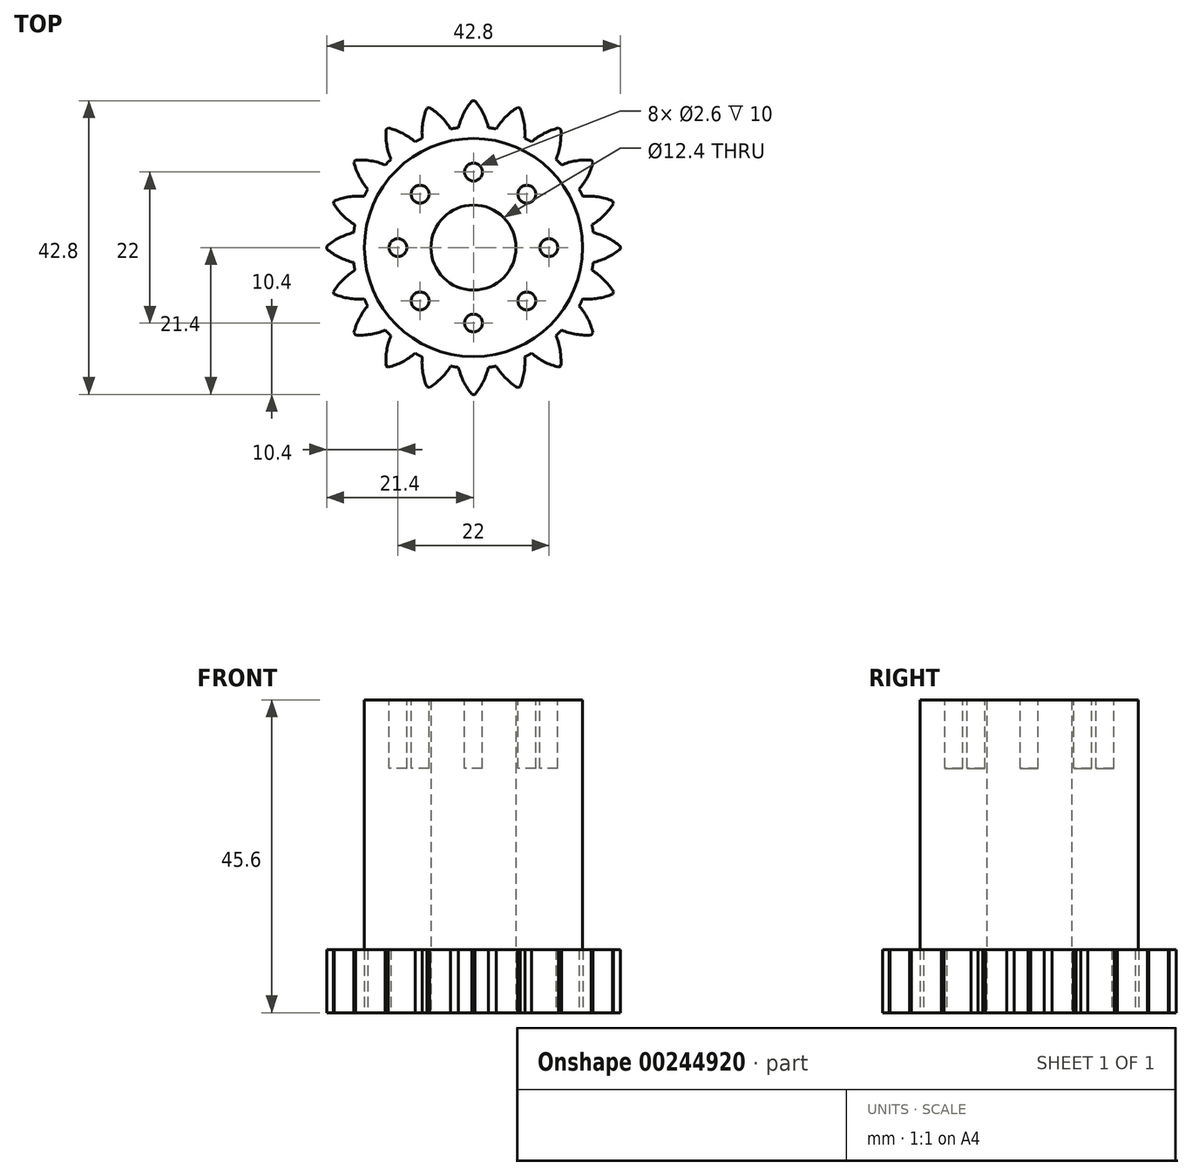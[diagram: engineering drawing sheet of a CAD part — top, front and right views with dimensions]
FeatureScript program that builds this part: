
annotation { "Feature Type Name" : "Feature", "Feature Type Description" : "" }
export const myFeature = defineFeature(function(context is Context, id is Id, definition is map)
    precondition{}
    {
        {
            var Q0;
            Q0=qCreatedBy(makeId("Top.planeOp"),FACE);
            var sketch = newSketch(context, id + "F0", { "sketchPlane" : qUnion([Q0])});
            skCircle(sketch, "E0", {"center": v(0, 0) * mm, "radius": 6.2 * mm});
            skCircle(sketch, "E1", {"center": v(0, 0) * mm, "radius": 15.9 * mm});
            skSolve(sketch);
        }
        {
            var Q0;
            Q0 = qSketchRegion(id + "F0", true);
            extrude(context, id + "F1", {"entities" : qUnion([Q0]), "depth" : 45.6 * mm, "offsetDistance" : 25 * mm});
        }
        {
            var Q0;
            Q0=makeQuery(id+"F1.opExtrude","CAP_FACE",FACE,{"disambiguationData":[OSD([sQuery(id+"F0.wireOp",EDGE,"E0"),sQuery(id+"F0.wireOp",EDGE,"E1")])],"isStart":false});
            var sketch = newSketch(context, id + "F2", { "sketchPlane" : qUnion([Q0])});
            skCircle(sketch, "E2", {"center": v(11, 0) * mm, "radius": 1.3 * mm});
            skCircle(sketch, "E3.1.0", {"center": v(7.78, 7.78) * mm, "radius": 1.3 * mm});
            skCircle(sketch, "E3.2.0", {"center": v(0, 11) * mm, "radius": 1.3 * mm});
            skCircle(sketch, "E3.3.0", {"center": v(-7.78, 7.78) * mm, "radius": 1.3 * mm});
            skPoint(sketch, "E3.center", {"position": v(0, 0) * mm});
            skCircle(sketch, "E4.1.4.0", {"center": v(-11, 0) * mm, "radius": 1.3 * mm});
            skCircle(sketch, "E4.1.5.0", {"center": v(-7.78, -7.78) * mm, "radius": 1.3 * mm});
            skCircle(sketch, "E4.1.6.0", {"center": v(0, -11) * mm, "radius": 1.3 * mm});
            skCircle(sketch, "E4.1.7.0", {"center": v(7.78, -7.78) * mm, "radius": 1.3 * mm});
            skSolve(sketch);
        }
        {
            var Q0;
            Q0 = qSketchRegion(id + "F2", true);
            extrude(context, id + "F3", {"entities" : qUnion([Q0]), "operationType" : NewBodyOperationType.REMOVE, "oppositeDirection" : true, "depth" : 10 * mm, "offsetDistance" : 25 * mm});
        }
        {
            var Q0;
            Q0=qCreatedBy(makeId("Top.planeOp"),FACE);
            var sketch = newSketch(context, id + "F4", { "sketchPlane" : qUnion([Q0])});
            skCircle(sketch, "E5", {"center": v(0, 0) * mm, "radius": 17.6 * mm});
            skCircle(sketch, "E6", {"center": v(0, 0) * mm, "radius": 6.2 * mm});
            skSolve(sketch);
        }
        {
            var Q0;
            Q0 = qSketchRegion(id + "F4", true);
            extrude(context, id + "F5", {"entities" : qUnion([Q0]), "operationType" : NewBodyOperationType.ADD, "depth" : 9.2 * mm, "offsetDistance" : 25 * mm});
        }
        {
            var Q0;
            Q0=qCreatedBy(makeId("Top.planeOp"),FACE);
            var sketch = newSketch(context, id + "F6", { "sketchPlane" : qUnion([Q0])});
            skLineSegment(sketch, "E7", {"start": v(21.4, 0) * mm, "end": v(17.4, 0) * mm});
            skLineSegment(sketch, "E8", {"start": v(21.4, 0) * mm, "end": v(21.4, 0.2) * mm});
            skLineSegment(sketch, "E9", {"start": v(17.4, 0) * mm, "end": v(17.4, 2.2) * mm});
            skArc(sketch, "E10", {"start": v(21.4, 0.2) * mm, "mid": v(19.52, 1.44) * mm, "end": v(17.4, 2.2) * mm});
            skArc(sketch, "E11.MirrorCS", {"start": v(21.4, -0.2) * mm, "mid": v(19.52, -1.44) * mm, "end": v(17.4, -2.2) * mm});
            skLineSegment(sketch, "E12.MirrorCS", {"start": v(21.4, 0) * mm, "end": v(21.4, -0.2) * mm});
            skLineSegment(sketch, "E13.MirrorCS", {"start": v(17.4, 0) * mm, "end": v(17.4, -2.2) * mm});
            skLineSegment(sketch, "E14.1.0", {"start": v(16.55, 5.38) * mm, "end": v(17.23, 3.28) * mm});
            skArc(sketch, "E14.1.1", {"start": v(20.3, 6.8) * mm, "mid": v(18.12, 7.4) * mm, "end": v(15.87, 7.47) * mm});
            skArc(sketch, "E14.1.2", {"start": v(20.41, 6.42) * mm, "mid": v(19, 4.67) * mm, "end": v(17.23, 3.28) * mm});
            skLineSegment(sketch, "E14.1.3", {"start": v(20.35, 6.61) * mm, "end": v(16.55, 5.38) * mm});
            skLineSegment(sketch, "E14.1.4", {"start": v(16.55, 5.38) * mm, "end": v(15.87, 7.47) * mm});
            skLineSegment(sketch, "E14.1.5", {"start": v(20.35, 6.61) * mm, "end": v(16.55, 5.38) * mm});
            skLineSegment(sketch, "E14.1.6", {"start": v(20.35, 6.61) * mm, "end": v(20.3, 6.8) * mm});
            skLineSegment(sketch, "E14.1.7", {"start": v(20.35, 6.61) * mm, "end": v(20.41, 6.42) * mm});
            skLineSegment(sketch, "E14.2.0", {"start": v(14.08, 10.23) * mm, "end": v(15.37, 8.45) * mm});
            skArc(sketch, "E14.2.1", {"start": v(17.2, 12.74) * mm, "mid": v(14.95, 12.63) * mm, "end": v(12.78, 12) * mm});
            skArc(sketch, "E14.2.2", {"start": v(17.43, 12.42) * mm, "mid": v(16.63, 10.31) * mm, "end": v(15.37, 8.45) * mm});
            skLineSegment(sketch, "E14.2.3", {"start": v(17.31, 12.58) * mm, "end": v(14.08, 10.23) * mm});
            skLineSegment(sketch, "E14.2.4", {"start": v(14.08, 10.23) * mm, "end": v(12.78, 12) * mm});
            skLineSegment(sketch, "E14.2.5", {"start": v(17.31, 12.58) * mm, "end": v(14.08, 10.23) * mm});
            skLineSegment(sketch, "E14.2.6", {"start": v(17.31, 12.58) * mm, "end": v(17.2, 12.74) * mm});
            skLineSegment(sketch, "E14.2.7", {"start": v(17.31, 12.58) * mm, "end": v(17.43, 12.42) * mm});
            skLineSegment(sketch, "E14.3.0", {"start": v(10.23, 14.08) * mm, "end": v(12, 12.78) * mm});
            skArc(sketch, "E14.3.1", {"start": v(12.42, 17.43) * mm, "mid": v(10.31, 16.63) * mm, "end": v(8.45, 15.37) * mm});
            skArc(sketch, "E14.3.2", {"start": v(12.74, 17.2) * mm, "mid": v(12.63, 14.95) * mm, "end": v(12, 12.78) * mm});
            skLineSegment(sketch, "E14.3.3", {"start": v(12.58, 17.31) * mm, "end": v(10.23, 14.08) * mm});
            skLineSegment(sketch, "E14.3.4", {"start": v(10.23, 14.08) * mm, "end": v(8.45, 15.37) * mm});
            skLineSegment(sketch, "E14.3.5", {"start": v(12.58, 17.31) * mm, "end": v(10.23, 14.08) * mm});
            skLineSegment(sketch, "E14.3.6", {"start": v(12.58, 17.31) * mm, "end": v(12.42, 17.43) * mm});
            skLineSegment(sketch, "E14.3.7", {"start": v(12.58, 17.31) * mm, "end": v(12.74, 17.2) * mm});
            skLineSegment(sketch, "E14.4.0", {"start": v(5.38, 16.55) * mm, "end": v(7.47, 15.87) * mm});
            skArc(sketch, "E14.4.1", {"start": v(6.42, 20.41) * mm, "mid": v(4.67, 19) * mm, "end": v(3.28, 17.23) * mm});
            skArc(sketch, "E14.4.2", {"start": v(6.8, 20.3) * mm, "mid": v(7.4, 18.12) * mm, "end": v(7.47, 15.87) * mm});
            skLineSegment(sketch, "E14.4.3", {"start": v(6.61, 20.35) * mm, "end": v(5.38, 16.55) * mm});
            skLineSegment(sketch, "E14.4.4", {"start": v(5.38, 16.55) * mm, "end": v(3.28, 17.23) * mm});
            skLineSegment(sketch, "E14.4.5", {"start": v(6.61, 20.35) * mm, "end": v(5.38, 16.55) * mm});
            skLineSegment(sketch, "E14.4.6", {"start": v(6.61, 20.35) * mm, "end": v(6.42, 20.41) * mm});
            skLineSegment(sketch, "E14.4.7", {"start": v(6.61, 20.35) * mm, "end": v(6.8, 20.3) * mm});
            skLineSegment(sketch, "E14.5.0", {"start": v(0, 17.4) * mm, "end": v(2.2, 17.4) * mm});
            skArc(sketch, "E14.5.1", {"start": v(-0.2, 21.4) * mm, "mid": v(-1.44, 19.52) * mm, "end": v(-2.2, 17.4) * mm});
            skArc(sketch, "E14.5.2", {"start": v(0.2, 21.4) * mm, "mid": v(1.44, 19.52) * mm, "end": v(2.2, 17.4) * mm});
            skLineSegment(sketch, "E14.5.3", {"start": v(0, 21.4) * mm, "end": v(0, 17.4) * mm});
            skLineSegment(sketch, "E14.5.4", {"start": v(0, 17.4) * mm, "end": v(-2.2, 17.4) * mm});
            skLineSegment(sketch, "E14.5.5", {"start": v(0, 21.4) * mm, "end": v(0, 17.4) * mm});
            skLineSegment(sketch, "E14.5.6", {"start": v(0, 21.4) * mm, "end": v(-0.2, 21.4) * mm});
            skLineSegment(sketch, "E14.5.7", {"start": v(0, 21.4) * mm, "end": v(0.2, 21.4) * mm});
            skLineSegment(sketch, "E14.6.0", {"start": v(-5.38, 16.55) * mm, "end": v(-3.28, 17.23) * mm});
            skArc(sketch, "E14.6.1", {"start": v(-6.8, 20.3) * mm, "mid": v(-7.4, 18.12) * mm, "end": v(-7.47, 15.87) * mm});
            skArc(sketch, "E14.6.2", {"start": v(-6.42, 20.41) * mm, "mid": v(-4.67, 19) * mm, "end": v(-3.28, 17.23) * mm});
            skLineSegment(sketch, "E14.6.3", {"start": v(-6.61, 20.35) * mm, "end": v(-5.38, 16.55) * mm});
            skLineSegment(sketch, "E14.6.4", {"start": v(-5.38, 16.55) * mm, "end": v(-7.47, 15.87) * mm});
            skLineSegment(sketch, "E14.6.5", {"start": v(-6.61, 20.35) * mm, "end": v(-5.38, 16.55) * mm});
            skLineSegment(sketch, "E14.6.6", {"start": v(-6.61, 20.35) * mm, "end": v(-6.8, 20.3) * mm});
            skLineSegment(sketch, "E14.6.7", {"start": v(-6.61, 20.35) * mm, "end": v(-6.42, 20.41) * mm});
            skLineSegment(sketch, "E14.7.0", {"start": v(-10.23, 14.08) * mm, "end": v(-8.45, 15.37) * mm});
            skArc(sketch, "E14.7.1", {"start": v(-12.74, 17.2) * mm, "mid": v(-12.63, 14.95) * mm, "end": v(-12, 12.78) * mm});
            skArc(sketch, "E14.7.2", {"start": v(-12.42, 17.43) * mm, "mid": v(-10.31, 16.63) * mm, "end": v(-8.45, 15.37) * mm});
            skLineSegment(sketch, "E14.7.3", {"start": v(-12.58, 17.31) * mm, "end": v(-10.23, 14.08) * mm});
            skLineSegment(sketch, "E14.7.4", {"start": v(-10.23, 14.08) * mm, "end": v(-12, 12.78) * mm});
            skLineSegment(sketch, "E14.7.5", {"start": v(-12.58, 17.31) * mm, "end": v(-10.23, 14.08) * mm});
            skLineSegment(sketch, "E14.7.6", {"start": v(-12.58, 17.31) * mm, "end": v(-12.74, 17.2) * mm});
            skLineSegment(sketch, "E14.7.7", {"start": v(-12.58, 17.31) * mm, "end": v(-12.42, 17.43) * mm});
            skLineSegment(sketch, "E14.8.0", {"start": v(-14.08, 10.23) * mm, "end": v(-12.78, 12) * mm});
            skArc(sketch, "E14.8.1", {"start": v(-17.43, 12.42) * mm, "mid": v(-16.63, 10.31) * mm, "end": v(-15.37, 8.45) * mm});
            skArc(sketch, "E14.8.2", {"start": v(-17.2, 12.74) * mm, "mid": v(-14.95, 12.63) * mm, "end": v(-12.78, 12) * mm});
            skLineSegment(sketch, "E14.8.3", {"start": v(-17.31, 12.58) * mm, "end": v(-14.08, 10.23) * mm});
            skLineSegment(sketch, "E14.8.4", {"start": v(-14.08, 10.23) * mm, "end": v(-15.37, 8.45) * mm});
            skLineSegment(sketch, "E14.8.5", {"start": v(-17.31, 12.58) * mm, "end": v(-14.08, 10.23) * mm});
            skLineSegment(sketch, "E14.8.6", {"start": v(-17.31, 12.58) * mm, "end": v(-17.43, 12.42) * mm});
            skLineSegment(sketch, "E14.8.7", {"start": v(-17.31, 12.58) * mm, "end": v(-17.2, 12.74) * mm});
            skLineSegment(sketch, "E14.9.0", {"start": v(-16.55, 5.38) * mm, "end": v(-15.87, 7.47) * mm});
            skArc(sketch, "E14.9.1", {"start": v(-20.41, 6.42) * mm, "mid": v(-19, 4.67) * mm, "end": v(-17.23, 3.28) * mm});
            skArc(sketch, "E14.9.2", {"start": v(-20.3, 6.8) * mm, "mid": v(-18.12, 7.4) * mm, "end": v(-15.87, 7.47) * mm});
            skLineSegment(sketch, "E14.9.3", {"start": v(-20.35, 6.61) * mm, "end": v(-16.55, 5.38) * mm});
            skLineSegment(sketch, "E14.9.4", {"start": v(-16.55, 5.38) * mm, "end": v(-17.23, 3.28) * mm});
            skLineSegment(sketch, "E14.9.5", {"start": v(-20.35, 6.61) * mm, "end": v(-16.55, 5.38) * mm});
            skLineSegment(sketch, "E14.9.6", {"start": v(-20.35, 6.61) * mm, "end": v(-20.41, 6.42) * mm});
            skLineSegment(sketch, "E14.9.7", {"start": v(-20.35, 6.61) * mm, "end": v(-20.3, 6.8) * mm});
            skLineSegment(sketch, "E14.10.0", {"start": v(-17.4, 0) * mm, "end": v(-17.4, 2.2) * mm});
            skArc(sketch, "E14.10.1", {"start": v(-21.4, -0.2) * mm, "mid": v(-19.52, -1.44) * mm, "end": v(-17.4, -2.2) * mm});
            skArc(sketch, "E14.10.2", {"start": v(-21.4, 0.2) * mm, "mid": v(-19.52, 1.44) * mm, "end": v(-17.4, 2.2) * mm});
            skLineSegment(sketch, "E14.10.3", {"start": v(-21.4, 0) * mm, "end": v(-17.4, 0) * mm});
            skLineSegment(sketch, "E14.10.4", {"start": v(-17.4, 0) * mm, "end": v(-17.4, -2.2) * mm});
            skLineSegment(sketch, "E14.10.5", {"start": v(-21.4, 0) * mm, "end": v(-17.4, 0) * mm});
            skLineSegment(sketch, "E14.10.6", {"start": v(-21.4, 0) * mm, "end": v(-21.4, -0.2) * mm});
            skLineSegment(sketch, "E14.10.7", {"start": v(-21.4, 0) * mm, "end": v(-21.4, 0.2) * mm});
            skLineSegment(sketch, "E14.11.0", {"start": v(-16.55, -5.38) * mm, "end": v(-17.23, -3.28) * mm});
            skArc(sketch, "E14.11.1", {"start": v(-20.3, -6.8) * mm, "mid": v(-18.12, -7.4) * mm, "end": v(-15.87, -7.47) * mm});
            skArc(sketch, "E14.11.2", {"start": v(-20.41, -6.42) * mm, "mid": v(-19, -4.67) * mm, "end": v(-17.23, -3.28) * mm});
            skLineSegment(sketch, "E14.11.3", {"start": v(-20.35, -6.61) * mm, "end": v(-16.55, -5.38) * mm});
            skLineSegment(sketch, "E14.11.4", {"start": v(-16.55, -5.38) * mm, "end": v(-15.87, -7.47) * mm});
            skLineSegment(sketch, "E14.11.5", {"start": v(-20.35, -6.61) * mm, "end": v(-16.55, -5.38) * mm});
            skLineSegment(sketch, "E14.11.6", {"start": v(-20.35, -6.61) * mm, "end": v(-20.3, -6.8) * mm});
            skLineSegment(sketch, "E14.11.7", {"start": v(-20.35, -6.61) * mm, "end": v(-20.41, -6.42) * mm});
            skLineSegment(sketch, "E14.12.0", {"start": v(-14.08, -10.23) * mm, "end": v(-15.37, -8.45) * mm});
            skArc(sketch, "E14.12.1", {"start": v(-17.2, -12.74) * mm, "mid": v(-14.95, -12.63) * mm, "end": v(-12.78, -12) * mm});
            skArc(sketch, "E14.12.2", {"start": v(-17.43, -12.42) * mm, "mid": v(-16.63, -10.31) * mm, "end": v(-15.37, -8.45) * mm});
            skLineSegment(sketch, "E14.12.3", {"start": v(-17.31, -12.58) * mm, "end": v(-14.08, -10.23) * mm});
            skLineSegment(sketch, "E14.12.4", {"start": v(-14.08, -10.23) * mm, "end": v(-12.78, -12) * mm});
            skLineSegment(sketch, "E14.12.5", {"start": v(-17.31, -12.58) * mm, "end": v(-14.08, -10.23) * mm});
            skLineSegment(sketch, "E14.12.6", {"start": v(-17.31, -12.58) * mm, "end": v(-17.2, -12.74) * mm});
            skLineSegment(sketch, "E14.12.7", {"start": v(-17.31, -12.58) * mm, "end": v(-17.43, -12.42) * mm});
            skLineSegment(sketch, "E14.13.0", {"start": v(-10.23, -14.08) * mm, "end": v(-12, -12.78) * mm});
            skArc(sketch, "E14.13.1", {"start": v(-12.42, -17.43) * mm, "mid": v(-10.31, -16.63) * mm, "end": v(-8.45, -15.37) * mm});
            skArc(sketch, "E14.13.2", {"start": v(-12.74, -17.2) * mm, "mid": v(-12.63, -14.95) * mm, "end": v(-12, -12.78) * mm});
            skLineSegment(sketch, "E14.13.3", {"start": v(-12.58, -17.31) * mm, "end": v(-10.23, -14.08) * mm});
            skLineSegment(sketch, "E14.13.4", {"start": v(-10.23, -14.08) * mm, "end": v(-8.45, -15.37) * mm});
            skLineSegment(sketch, "E14.13.5", {"start": v(-12.58, -17.31) * mm, "end": v(-10.23, -14.08) * mm});
            skLineSegment(sketch, "E14.13.6", {"start": v(-12.58, -17.31) * mm, "end": v(-12.42, -17.43) * mm});
            skLineSegment(sketch, "E14.13.7", {"start": v(-12.58, -17.31) * mm, "end": v(-12.74, -17.2) * mm});
            skLineSegment(sketch, "E14.14.0", {"start": v(-5.38, -16.55) * mm, "end": v(-7.47, -15.87) * mm});
            skArc(sketch, "E14.14.1", {"start": v(-6.42, -20.41) * mm, "mid": v(-4.67, -19) * mm, "end": v(-3.28, -17.23) * mm});
            skArc(sketch, "E14.14.2", {"start": v(-6.8, -20.3) * mm, "mid": v(-7.4, -18.12) * mm, "end": v(-7.47, -15.87) * mm});
            skLineSegment(sketch, "E14.14.3", {"start": v(-6.61, -20.35) * mm, "end": v(-5.38, -16.55) * mm});
            skLineSegment(sketch, "E14.14.4", {"start": v(-5.38, -16.55) * mm, "end": v(-3.28, -17.23) * mm});
            skLineSegment(sketch, "E14.14.5", {"start": v(-6.61, -20.35) * mm, "end": v(-5.38, -16.55) * mm});
            skLineSegment(sketch, "E14.14.6", {"start": v(-6.61, -20.35) * mm, "end": v(-6.42, -20.41) * mm});
            skLineSegment(sketch, "E14.14.7", {"start": v(-6.61, -20.35) * mm, "end": v(-6.8, -20.3) * mm});
            skLineSegment(sketch, "E14.15.0", {"start": v(0, -17.4) * mm, "end": v(-2.2, -17.4) * mm});
            skArc(sketch, "E14.15.1", {"start": v(0.2, -21.4) * mm, "mid": v(1.44, -19.52) * mm, "end": v(2.2, -17.4) * mm});
            skArc(sketch, "E14.15.2", {"start": v(-0.2, -21.4) * mm, "mid": v(-1.44, -19.52) * mm, "end": v(-2.2, -17.4) * mm});
            skLineSegment(sketch, "E14.15.3", {"start": v(0, -21.4) * mm, "end": v(0, -17.4) * mm});
            skLineSegment(sketch, "E14.15.4", {"start": v(0, -17.4) * mm, "end": v(2.2, -17.4) * mm});
            skLineSegment(sketch, "E14.15.5", {"start": v(0, -21.4) * mm, "end": v(0, -17.4) * mm});
            skLineSegment(sketch, "E14.15.6", {"start": v(0, -21.4) * mm, "end": v(0.2, -21.4) * mm});
            skLineSegment(sketch, "E14.15.7", {"start": v(0, -21.4) * mm, "end": v(-0.2, -21.4) * mm});
            skLineSegment(sketch, "E14.16.0", {"start": v(5.38, -16.55) * mm, "end": v(3.28, -17.23) * mm});
            skArc(sketch, "E14.16.1", {"start": v(6.8, -20.3) * mm, "mid": v(7.4, -18.12) * mm, "end": v(7.47, -15.87) * mm});
            skArc(sketch, "E14.16.2", {"start": v(6.42, -20.41) * mm, "mid": v(4.67, -19) * mm, "end": v(3.28, -17.23) * mm});
            skLineSegment(sketch, "E14.16.3", {"start": v(6.61, -20.35) * mm, "end": v(5.38, -16.55) * mm});
            skLineSegment(sketch, "E14.16.4", {"start": v(5.38, -16.55) * mm, "end": v(7.47, -15.87) * mm});
            skLineSegment(sketch, "E14.16.5", {"start": v(6.61, -20.35) * mm, "end": v(5.38, -16.55) * mm});
            skLineSegment(sketch, "E14.16.6", {"start": v(6.61, -20.35) * mm, "end": v(6.8, -20.3) * mm});
            skLineSegment(sketch, "E14.16.7", {"start": v(6.61, -20.35) * mm, "end": v(6.42, -20.41) * mm});
            skLineSegment(sketch, "E14.17.0", {"start": v(10.23, -14.08) * mm, "end": v(8.45, -15.37) * mm});
            skArc(sketch, "E14.17.1", {"start": v(12.74, -17.2) * mm, "mid": v(12.63, -14.95) * mm, "end": v(12, -12.78) * mm});
            skArc(sketch, "E14.17.2", {"start": v(12.42, -17.43) * mm, "mid": v(10.31, -16.63) * mm, "end": v(8.45, -15.37) * mm});
            skLineSegment(sketch, "E14.17.3", {"start": v(12.58, -17.31) * mm, "end": v(10.23, -14.08) * mm});
            skLineSegment(sketch, "E14.17.4", {"start": v(10.23, -14.08) * mm, "end": v(12, -12.78) * mm});
            skLineSegment(sketch, "E14.17.5", {"start": v(12.58, -17.31) * mm, "end": v(10.23, -14.08) * mm});
            skLineSegment(sketch, "E14.17.6", {"start": v(12.58, -17.31) * mm, "end": v(12.74, -17.2) * mm});
            skLineSegment(sketch, "E14.17.7", {"start": v(12.58, -17.31) * mm, "end": v(12.42, -17.43) * mm});
            skLineSegment(sketch, "E14.18.0", {"start": v(14.08, -10.23) * mm, "end": v(12.78, -12) * mm});
            skArc(sketch, "E14.18.1", {"start": v(17.43, -12.42) * mm, "mid": v(16.63, -10.31) * mm, "end": v(15.37, -8.45) * mm});
            skArc(sketch, "E14.18.2", {"start": v(17.2, -12.74) * mm, "mid": v(14.95, -12.63) * mm, "end": v(12.78, -12) * mm});
            skLineSegment(sketch, "E14.18.3", {"start": v(17.31, -12.58) * mm, "end": v(14.08, -10.23) * mm});
            skLineSegment(sketch, "E14.18.4", {"start": v(14.08, -10.23) * mm, "end": v(15.37, -8.45) * mm});
            skLineSegment(sketch, "E14.18.5", {"start": v(17.31, -12.58) * mm, "end": v(14.08, -10.23) * mm});
            skLineSegment(sketch, "E14.18.6", {"start": v(17.31, -12.58) * mm, "end": v(17.43, -12.42) * mm});
            skLineSegment(sketch, "E14.18.7", {"start": v(17.31, -12.58) * mm, "end": v(17.2, -12.74) * mm});
            skLineSegment(sketch, "E14.19.0", {"start": v(16.55, -5.38) * mm, "end": v(15.87, -7.47) * mm});
            skArc(sketch, "E14.19.1", {"start": v(20.41, -6.42) * mm, "mid": v(19, -4.67) * mm, "end": v(17.23, -3.28) * mm});
            skArc(sketch, "E14.19.2", {"start": v(20.3, -6.8) * mm, "mid": v(18.12, -7.4) * mm, "end": v(15.87, -7.47) * mm});
            skLineSegment(sketch, "E14.19.3", {"start": v(20.35, -6.61) * mm, "end": v(16.55, -5.38) * mm});
            skLineSegment(sketch, "E14.19.4", {"start": v(16.55, -5.38) * mm, "end": v(17.23, -3.28) * mm});
            skLineSegment(sketch, "E14.19.5", {"start": v(20.35, -6.61) * mm, "end": v(16.55, -5.38) * mm});
            skLineSegment(sketch, "E14.19.6", {"start": v(20.35, -6.61) * mm, "end": v(20.41, -6.42) * mm});
            skLineSegment(sketch, "E14.19.7", {"start": v(20.35, -6.61) * mm, "end": v(20.3, -6.8) * mm});
            skPoint(sketch, "E14.center", {"position": v(0, 0) * mm});
            skSolve(sketch);
        }
        {
            var Q0;
            Q0 = qSketchRegion(id + "F6", true);
            extrude(context, id + "F7", {"entities" : qUnion([Q0]), "operationType" : NewBodyOperationType.ADD, "depth" : 9.2 * mm, "offsetDistance" : 25 * mm});
        }
    });
